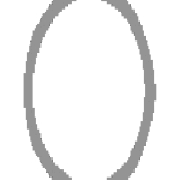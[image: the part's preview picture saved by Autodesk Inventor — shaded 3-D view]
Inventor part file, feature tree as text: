
AUTODESK INVENTOR PART (.ipt)
format: ipt  version: 2021 (Build 250183000, 183)  size: 110,080 bytes
history: native  units: in
note: dims shown in document units (in); Inventor stores cm internally (conversion verified against a paired STEP export)
features: other x4, sketch x3, plane x1
ambient origin geometry x8: Origin, YZ Plane, XZ Plane, XY Plane, X Axis, Y Axis, Z Axis, Center Point
bodies: Solid1 (feature_tree), Body (feature_tree)
feature tree (8):
  other  "Driven Length"
  other  "Frame Generator"
  other  "Start Plane"
  other  "End Plane"
  sketch  "Sketch"  dims[d2=16.0833in d4=-0.0in d5=16.0833in d6=0.12in d7=0.0in d8=90.0deg d9=16.0833in]
  sketch  "Sketch2"  dims[d0=1.0in]
  plane  "Work Plane3"
  sketch  "Sketch3"  dims[d1=0.065in]
